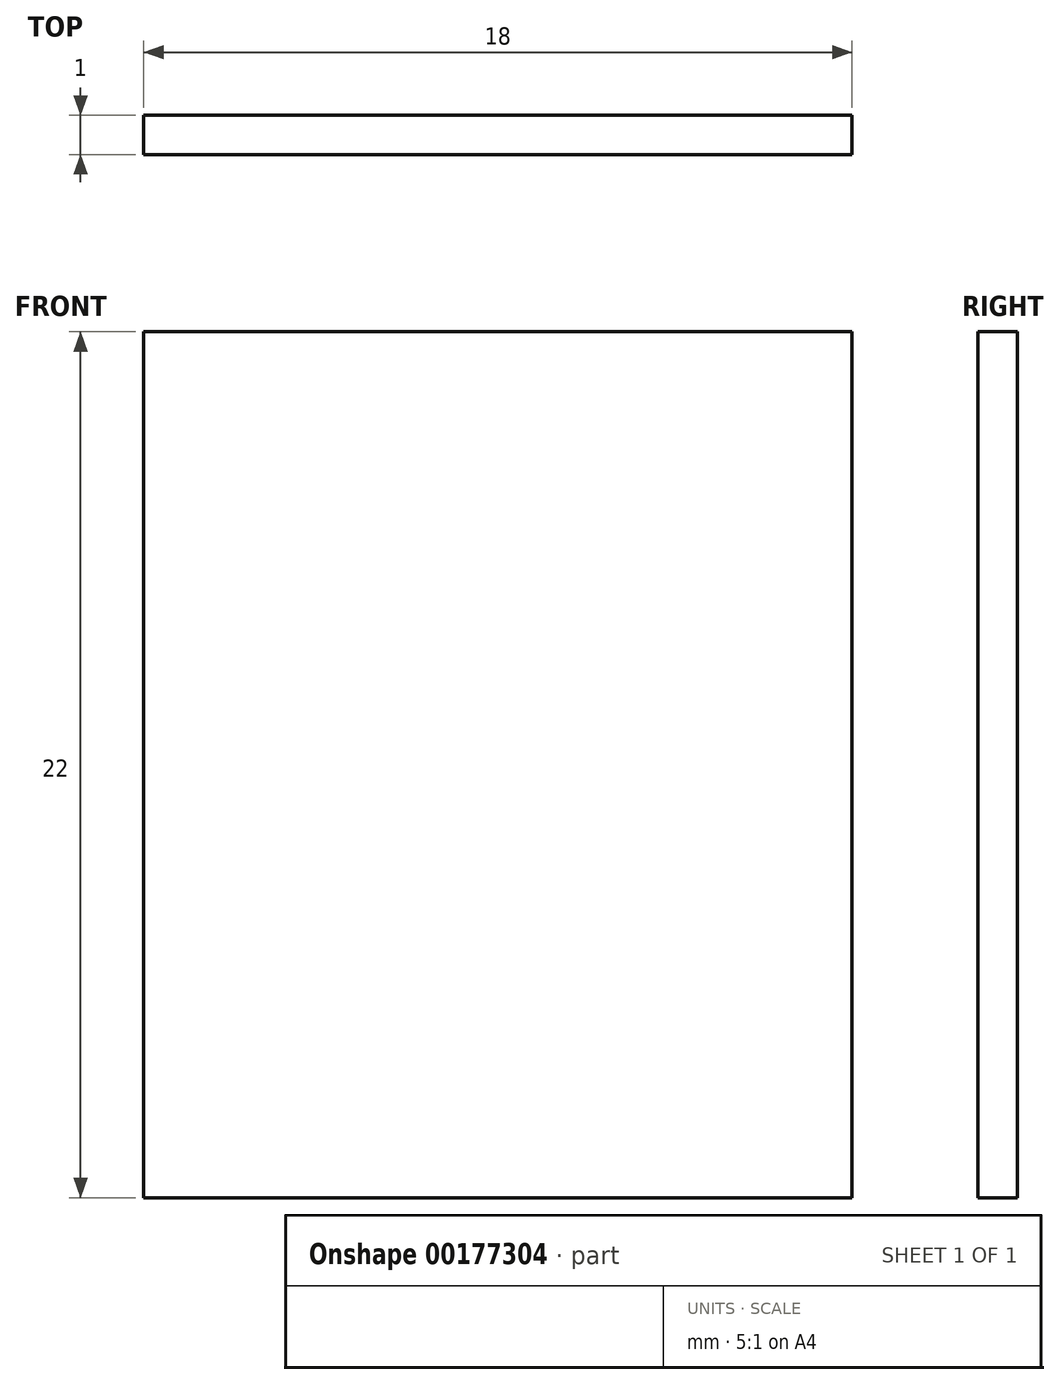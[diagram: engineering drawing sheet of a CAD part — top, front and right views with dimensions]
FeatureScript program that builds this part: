
annotation { "Feature Type Name" : "Feature", "Feature Type Description" : "" }
export const myFeature = defineFeature(function(context is Context, id is Id, definition is map)
    precondition{}
    {
        {
            var Q0;
            Q0=qCreatedBy(makeId("Front.planeOp"),FACE);
            var sketch = newSketch(context, id + "F0", { "sketchPlane" : qUnion([Q0])});
            skLineSegment(sketch, "E0.bottom", {"start": v(-9, 11) * mm, "end": v(9, 11) * mm});
            skLineSegment(sketch, "E0.top", {"start": v(-9, -11) * mm, "end": v(9, -11) * mm});
            skLineSegment(sketch, "E0.left", {"start": v(-9, 11) * mm, "end": v(-9, -11) * mm});
            skLineSegment(sketch, "E0.right", {"start": v(9, 11) * mm, "end": v(9, -11) * mm});
            skPoint(sketch, "E0.middle", {"position": v(0, 0) * mm});
            skSolve(sketch);
        }
        {
            var Q0;
            Q0 = qSketchRegion(id + "F0", true);
            extrude(context, id + "F1", {"entities" : qUnion([Q0]), "depth" : 1 * mm});
        }
    });
